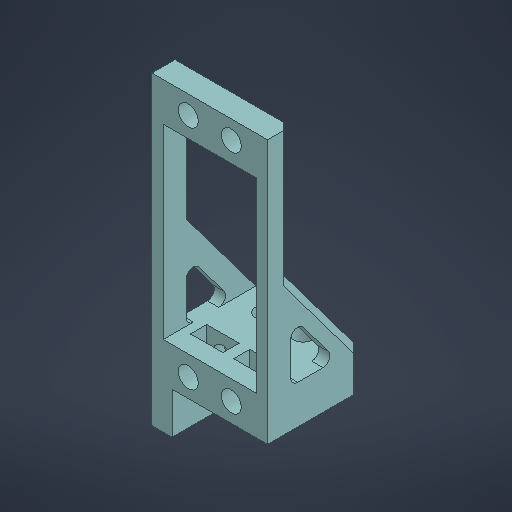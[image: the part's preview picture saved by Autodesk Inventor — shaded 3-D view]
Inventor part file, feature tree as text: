
AUTODESK INVENTOR PART (.ipt)
format: ipt  version: 2025.1 (Build 291241000, 241)  size: 668,672 bytes
history: native  units: in
note: dims shown in document units (in); Inventor stores cm internally (conversion verified against a paired STEP export)
features: extrude x10, sketch x5, chamfer x2, plane x1, mirror x1, fillet x1, projected_geometry x1
ambient origin geometry x8: Origin, YZ Plane, XZ Plane, XY Plane, X Axis, Y Axis, Z Axis, Center Point
bodies: Solid1 (feature_tree)
feature tree (21):
  sketch  "Sketch1"  dims[d0=1.5866in d1=0.7913in]
  extrude  "Extrusion1"  Depth=0.7913in
  extrude  "Extrusion2"  Depth=0.9843in
  extrude  "Extrusion3"  Depth=0.1713in
  sketch  "Sketch2"  dims[d2=2.2441in d3=0.9843in]
  extrude  "Extrusion4"  Depth=0.1575in
  extrude  "Extrusion5"  Depth=0.7874in
  sketch  "Sketch3"  dims[d4=0.1713in d5=0.1703in]
  extrude  "Extrusion6"  Depth=0.1969in TaperAngle=0.0deg
  extrude  "Extrusion7"  Depth=0.5906in TaperAngle=0.0deg
  extrude  "Extrusion8"  Depth=0.3937in TaperAngle=0.0deg
  plane  "Work Plane2"
  mirror  "Mirror1"
  fillet  "Fillet1"  Radius=0.0866in
  chamfer  "Chamfer1"  Distance=0.3268in
  extrude  "Extrusion9"  Depth=0.1575in
  extrude  "Extrusion10"  Depth=0.1575in
  chamfer  "Chamfer2"  Distance=0.3937in
  projected_geometry  "Projected Loop1"
  sketch  "Sketch4"  dims[d6=0.1713in d7=0.1575in d8=0.1713in]
  sketch  "Sketch5"  dims[d9=0.2126in d13=0.2126in d14=0.1969in d15=0.0in d16=0.5906in d17=0.0in d18=0.3937in d19=0.0in d20=0.0866in d21=0.3268in d22=0.1575in d23=0.1575in d24=0.3937in d25=0.0in d26=0.1181in d27=0.0in d28=1.9232in d29=0.3661in d30=0.3661in d31=0.1575in d35=0.3937in d36=0.0in d37=0.1713in d38=0.0in d39=0.0984in d41=0.3937in d42=1.4035in d43=0.0in d46=0.1969in d47=0.0591in d48=0.0591in d49=0.0787in d50=45.0deg d51=0.1575in d52=0.1181in d53=0.0in d54=0.2756in d55=0.1378in d56=0.1575in d57=0.3937in d58=0.0in d59=0.3543in d60=0.3543in d61=0.0787in d62=45.0deg d63=0.7874in]
